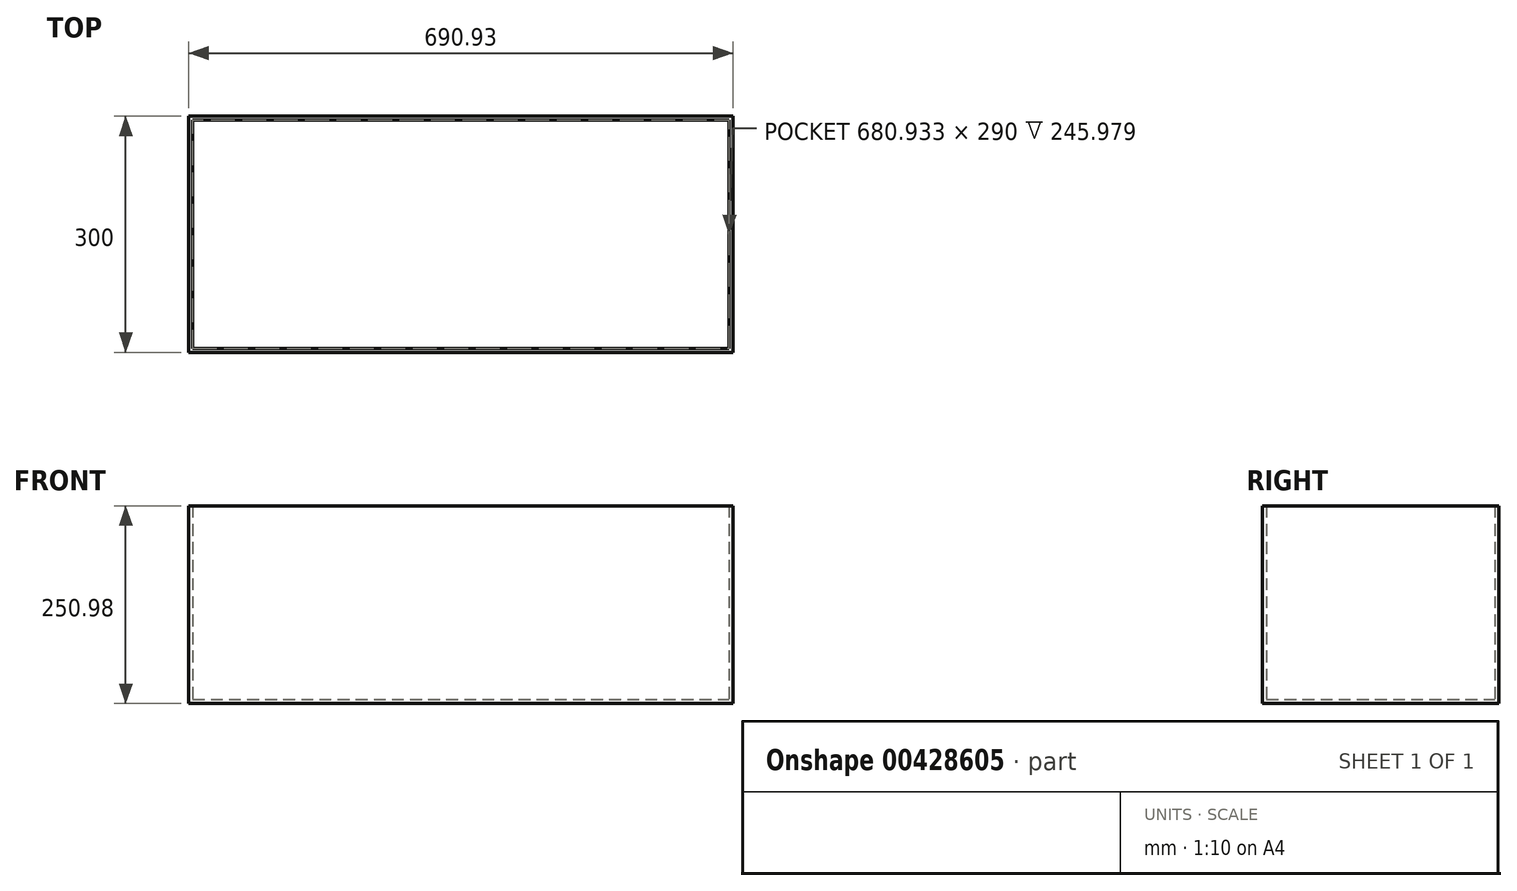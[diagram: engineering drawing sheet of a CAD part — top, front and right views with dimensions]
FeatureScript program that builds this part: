
annotation { "Feature Type Name" : "Feature", "Feature Type Description" : "" }
export const myFeature = defineFeature(function(context is Context, id is Id, definition is map)
    precondition{}
    {
        {
            var Q0;
            Q0=qCreatedBy(makeId("Front.planeOp"),FACE);
            var sketch = newSketch(context, id + "F0", { "sketchPlane" : qUnion([Q0])});
            skLineSegment(sketch, "E0.bottom", {"start": v(-42.93, -17.09) * mm, "end": v(48, -17.09) * mm});
            skLineSegment(sketch, "E0.top", {"start": v(-42.93, -68.07) * mm, "end": v(48, -68.07) * mm});
            skLineSegment(sketch, "E0.left", {"start": v(-42.93, -17.09) * mm, "end": v(-42.93, -68.07) * mm});
            skLineSegment(sketch, "E0.right", {"start": v(48, -17.09) * mm, "end": v(48, -68.07) * mm});
            skSolve(sketch);
        }
        {
            var Q0;
            Q0=makeQuery(id+"F0.imprint","IMPRINT",FACE,{"disambiguationData":[TD([[makeQuery(id+"F0.imprint","IMPRINT",EDGE,{"derivedFrom":sQuery(id+"F0.wireOp",EDGE,"E0.bottom")}),-1.0]])]});
            extrude(context, id + "F1", {"entities" : qUnion([Q0]), "depth" : 300 * mm});
        }
        {
            var Q0;
            Q0=makeQuery(id+"F1.opExtrude","SWEPT_FACE",FACE,{"disambiguationData":[OSD([sQuery(id+"F0.wireOp",EDGE,"E0.left")])]});
            extrude(context, id + "F2", {"entities" : qUnion([Q0]), "operationType" : NewBodyOperationType.ADD, "depth" : 600 * mm});
        }
        {
            var Q0;
            {var subQ0=sQuery(id+"F0.wireOp",EDGE,"E0.bottom");Q0=makeQuery(id+"F2.boolean.opBoolean","MERGE",FACE,{"derivedFrom":[makeQuery(id+"F1.opExtrude","SWEPT_FACE",FACE,{"disambiguationData":[OSD([subQ0])]}),makeQuery(id+"F2.opExtrude","SWEPT_FACE",FACE,{"disambiguationData":[OSD([subQ0,sQuery(id+"F0.wireOp",EDGE,"E0.left")])]})]});}
            extrude(context, id + "F3", {"entities" : qUnion([Q0]), "operationType" : NewBodyOperationType.ADD, "depth" : 200 * mm});
        }
        {
            var Q0;
            Q0=makeQuery(id+"F3.opExtrude","CAP_FACE",FACE,{"disambiguationData":[OSD([sQuery(id+"F0.wireOp",EDGE,"E0.bottom"),sQuery(id+"F0.wireOp",EDGE,"E0.left")])],"isStart":false});
            shell(context, id + "F4", {"entities" : qUnion([Q0]), "thickness" : 5 * mm});
        }
    });
